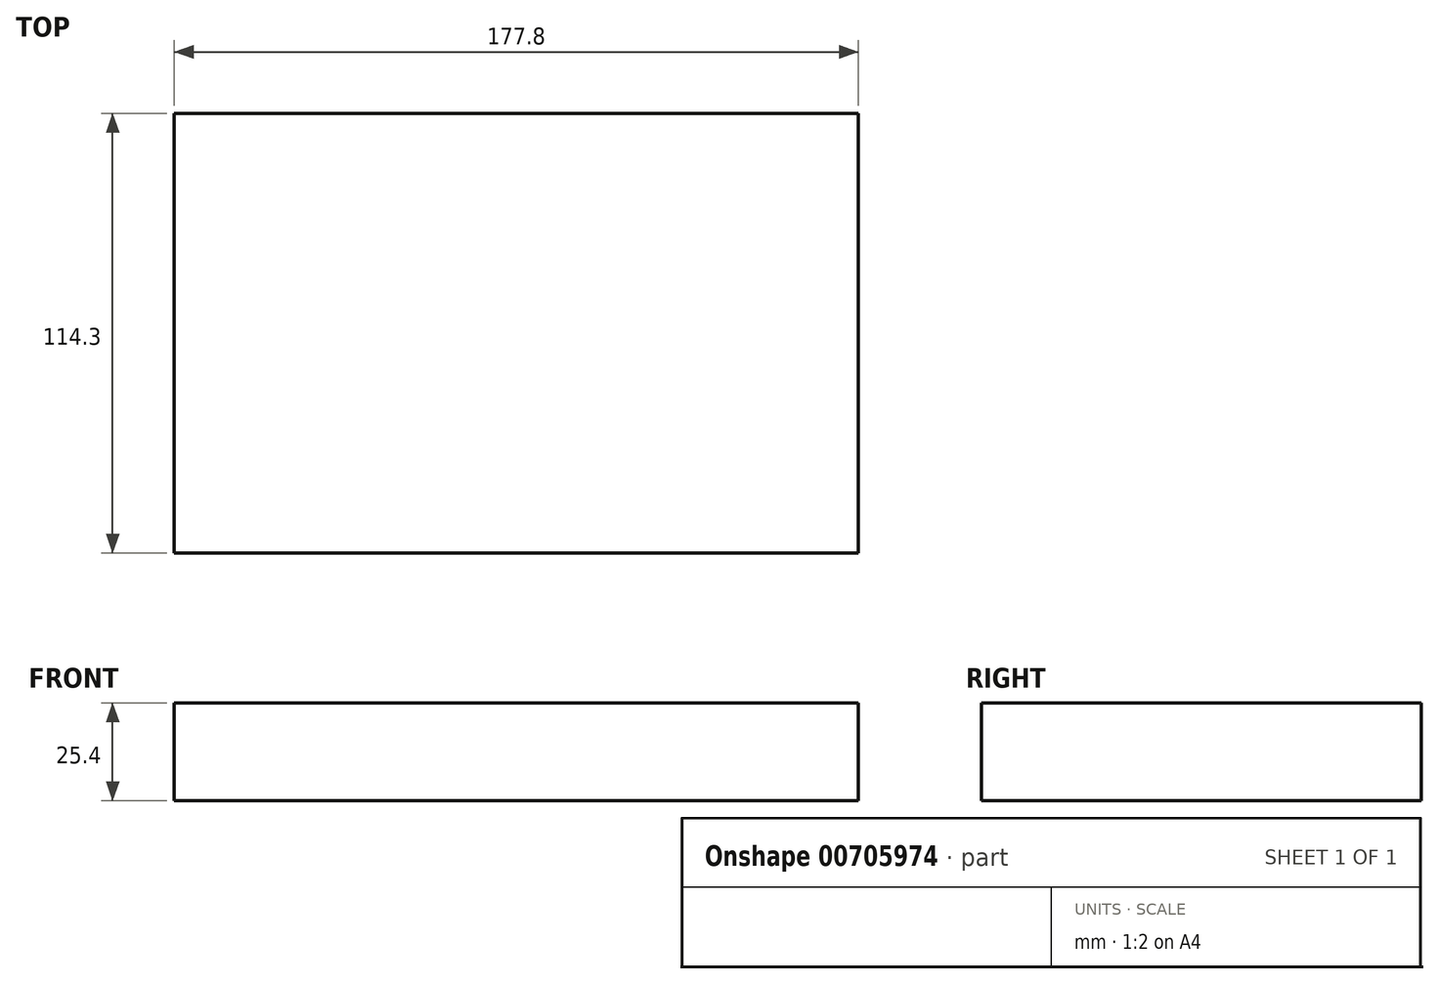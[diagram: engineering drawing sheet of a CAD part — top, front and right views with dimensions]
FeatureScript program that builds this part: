
annotation { "Feature Type Name" : "Feature", "Feature Type Description" : "" }
export const myFeature = defineFeature(function(context is Context, id is Id, definition is map)
    precondition{}
    {
        {
            var Q0;
            Q0=qCreatedBy(makeId("Top.planeOp"),FACE);
            var sketch = newSketch(context, id + "F0", { "sketchPlane" : qUnion([Q0])});
            skLineSegment(sketch, "E0.bottom", {"start": v(-90.68, 87.39) * mm, "end": v(87.12, 87.39) * mm});
            skLineSegment(sketch, "E0.top", {"start": v(-90.68, -26.91) * mm, "end": v(87.12, -26.91) * mm});
            skLineSegment(sketch, "E0.left", {"start": v(-90.68, 87.39) * mm, "end": v(-90.68, -26.91) * mm});
            skLineSegment(sketch, "E0.right", {"start": v(87.12, 87.39) * mm, "end": v(87.12, -26.91) * mm});
            skSolve(sketch);
        }
        {
            var Q0;
            Q0=makeQuery(id+"F0.imprint","IMPRINT",FACE,{"disambiguationData":[TD([[makeQuery(id+"F0.imprint","IMPRINT",EDGE,{"derivedFrom":sQuery(id+"F0.wireOp",EDGE,"E0.bottom")}),-1.0]])]});
            var sketch = newSketch(context, id + "F1", { "sketchPlane" : qUnion([Q0])});
            skSolve(sketch);
        }
        {
            var Q0;
            Q0=makeQuery(id+"F1.imprint","IMPRINT",FACE,{"disambiguationData":[TD([[makeQuery(id+"F1.imprint","IMPRINT",EDGE,{"derivedFrom":makeQuery(id+"F0.imprint","IMPRINT",EDGE,{"derivedFrom":sQuery(id+"F0.wireOp",EDGE,"E0.bottom")})}),-1.0]])]});
            extrude(context, id + "F2", {"entities" : qUnion([Q0]), "depth" : 25.4 * mm, "offsetDistance" : 25.4 * mm});
        }
    });
